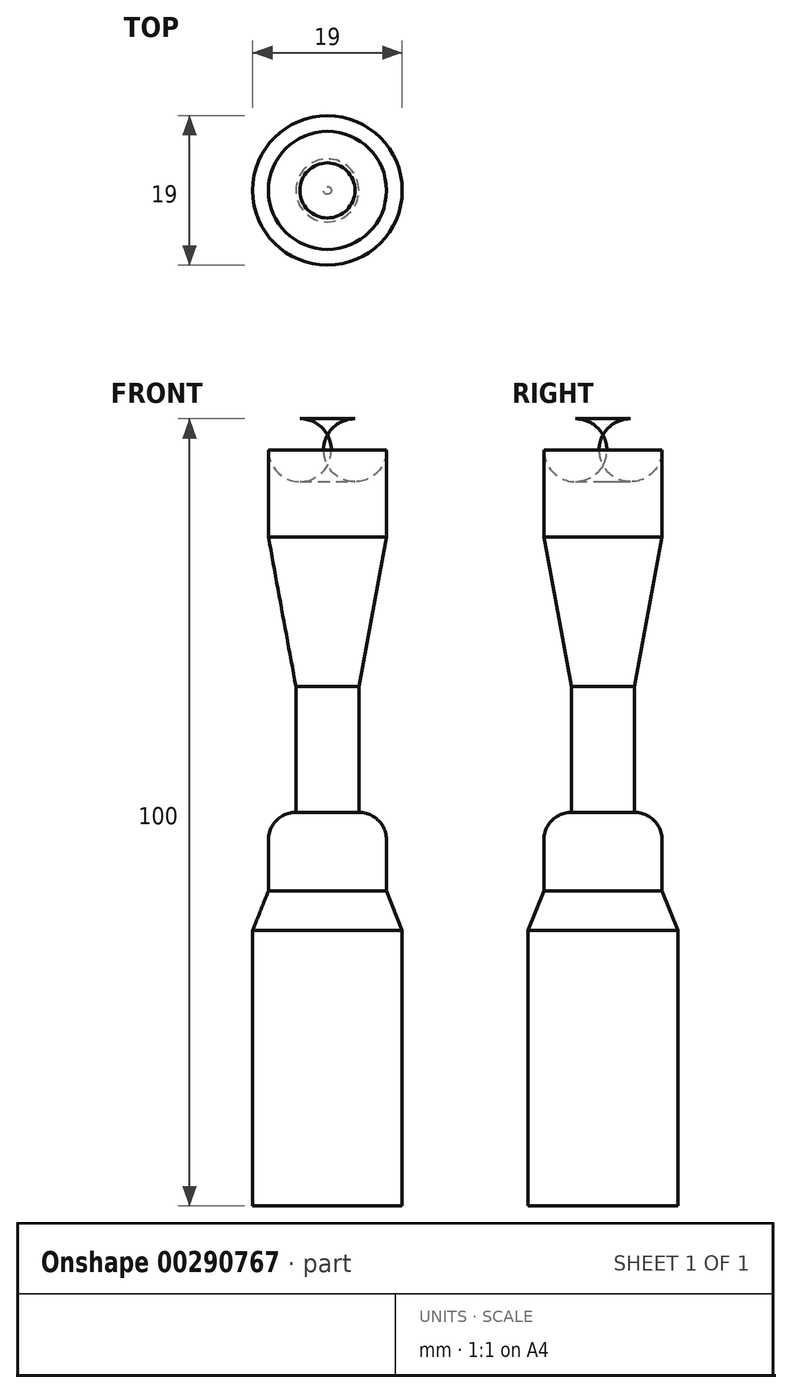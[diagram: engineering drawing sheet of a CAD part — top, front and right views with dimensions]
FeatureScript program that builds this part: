
annotation { "Feature Type Name" : "Feature", "Feature Type Description" : "" }
export const myFeature = defineFeature(function(context is Context, id is Id, definition is map)
    precondition{}
    {
        {
            var Q0;
            Q0=qCreatedBy(makeId("Front.planeOp"),FACE);
            var sketch = newSketch(context, id + "F0", { "sketchPlane" : qUnion([Q0])});
            skLineSegment(sketch, "E0", {"start": v(0, 0) * mm, "end": v(3.5, 0) * mm});
            skArc(sketch, "E1", {"start": v(7.5, -4) * mm, "mid": v(6.33, -1.17) * mm, "end": v(3.5, 0) * mm});
            skLineSegment(sketch, "E2", {"start": v(7.5, -4) * mm, "end": v(7.5, -15) * mm});
            skLineSegment(sketch, "E3", {"start": v(7.5, -15) * mm, "end": v(4, -34) * mm});
            skLineSegment(sketch, "E4", {"start": v(4, -34) * mm, "end": v(4, -50) * mm});
            skArc(sketch, "E5", {"start": v(7.5, -53.5) * mm, "mid": v(6.47, -51.03) * mm, "end": v(4, -50) * mm});
            skLineSegment(sketch, "E6", {"start": v(7.5, -60) * mm, "end": v(9.5, -65) * mm});
            skLineSegment(sketch, "E7", {"start": v(7.5, -53.5) * mm, "end": v(7.5, -60) * mm});
            skLineSegment(sketch, "E8", {"start": v(9.5, -100) * mm, "end": v(9.5, -65) * mm});
            skLineSegment(sketch, "E9", {"start": v(9.5, -100) * mm, "end": v(0, -100) * mm});
            skLineSegment(sketch, "E10", {"start": v(0, -100) * mm, "end": v(0, 0) * mm});
            skSolve(sketch);
        }
        {
            var Q0;
            Q0=makeQuery(id+"F0.imprint","IMPRINT",FACE,{"disambiguationData":[TD([[makeQuery(id+"F0.imprint","IMPRINT",EDGE,{"derivedFrom":sQuery(id+"F0.wireOp",EDGE,"E0")}),-1.0]])]});
            var Q1;
            Q1=sQuery(id+"F0.wireOp",EDGE,"E10");
            revolve(context, id + "F1", {"entities" : qUnion([Q0]), "axis" : qUnion([Q1]), "revolveType" : RevolveType.FULL});
        }
    });
